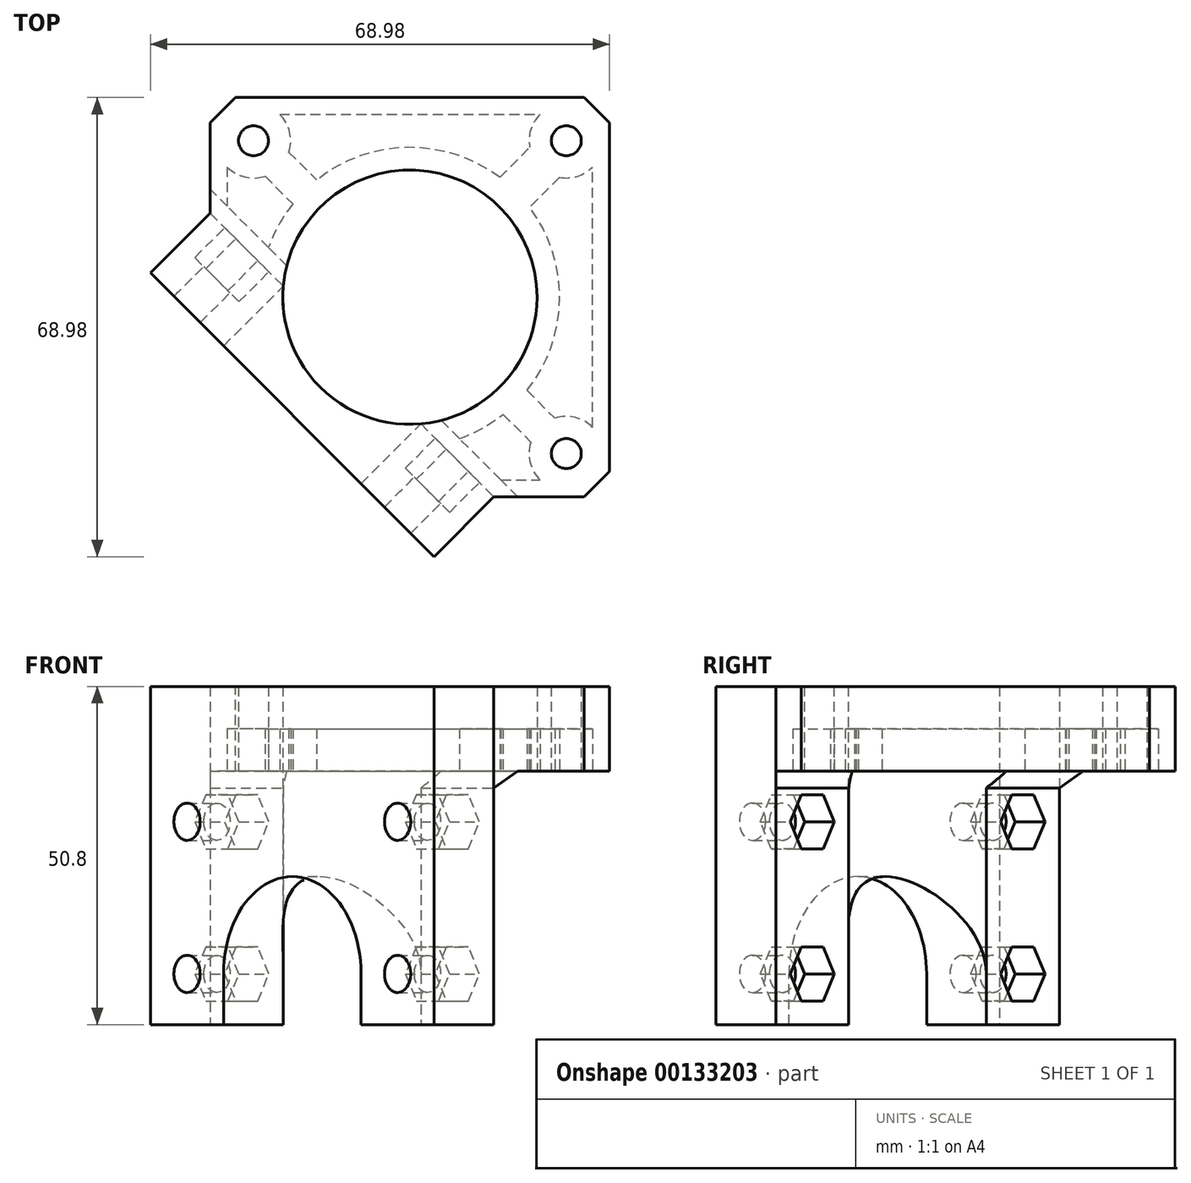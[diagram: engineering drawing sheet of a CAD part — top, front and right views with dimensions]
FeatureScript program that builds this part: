
annotation { "Feature Type Name" : "Feature", "Feature Type Description" : "" }
export const myFeature = defineFeature(function(context is Context, id is Id, definition is map)
    precondition{}
    {
        {
            var Q0;
            Q0=qCreatedBy(makeId("Top.planeOp"),FACE);
            var sketch = newSketch(context, id + "F0", { "sketchPlane" : qUnion([Q0])});
            skCircle(sketch, "E0", {"center": v(0, 0) * mm, "radius": 19.1 * mm});
            skLineSegment(sketch, "E1.bottom", {"start": v(-30, 30) * mm, "end": v(30, 30) * mm});
            skLineSegment(sketch, "E1.top", {"start": v(-30, -30) * mm, "end": v(30, -30) * mm});
            skLineSegment(sketch, "E1.left", {"start": v(-30, 30) * mm, "end": v(-30, -30) * mm});
            skLineSegment(sketch, "E1.right", {"start": v(30, 30) * mm, "end": v(30, -30) * mm});
            skCircle(sketch, "E2", {"center": v(-23.5, 23.5) * mm, "radius": 2.25 * mm});
            skCircle(sketch, "E3", {"center": v(-23.5, -23.5) * mm, "radius": 2.25 * mm});
            skCircle(sketch, "E4", {"center": v(23.5, -23.5) * mm, "radius": 2.25 * mm});
            skCircle(sketch, "E5", {"center": v(23.5, 23.5) * mm, "radius": 2.25 * mm});
            skLineSegment(sketch, "E6", {"start": v(0, -30) * mm, "end": v(0, 30) * mm, "construction": true});
            skLineSegment(sketch, "E7", {"start": v(-30, 0) * mm, "end": v(30, 0) * mm, "construction": true});
            skPoint(sketch, "E7.endSnap0", {"position": v(30, 0) * mm});
            skCircle(sketch, "E8", {"center": v(0, 0) * mm, "radius": 33.23 * mm, "construction": true});
            skSolve(sketch);
        }
        {
            var Q0;
            Q0=makeQuery(id+"F0.imprint","IMPRINT",FACE,{"disambiguationData":[TD([[makeQuery(id+"F0.imprint","IMPRINT",EDGE,{"derivedFrom":sQuery(id+"F0.wireOp",EDGE,"E0")}),-1.0]])]});
            extrude(context, id + "F1", {"entities" : qUnion([Q0]), "depth" : 50.8 * mm, "offsetDistance" : 25.4 * mm});
        }
        {
            var Q0;
            Q0=makeQuery(id+"F1.opExtrude","CAP_FACE",FACE,{"disambiguationData":[OSD([sQuery(id+"F0.wireOp",EDGE,"E0"),sQuery(id+"F0.wireOp",EDGE,"E1.bottom"),sQuery(id+"F0.wireOp",EDGE,"E1.top"),sQuery(id+"F0.wireOp",EDGE,"E1.left"),sQuery(id+"F0.wireOp",EDGE,"E1.right"),sQuery(id+"F0.wireOp",EDGE,"E2"),sQuery(id+"F0.wireOp",EDGE,"E3"),sQuery(id+"F0.wireOp",EDGE,"E4"),sQuery(id+"F0.wireOp",EDGE,"E5")])],"isStart":true});
            var sketch = newSketch(context, id + "F2", { "sketchPlane" : qUnion([Q0])});
            skLineSegment(sketch, "E9", {"start": v(-30, 5.35) * mm, "end": v(-5.35, 30) * mm});
            skLineSegment(sketch, "E10", {"start": v(-5.35, 30) * mm, "end": v(-30, 30) * mm});
            skLineSegment(sketch, "E11", {"start": v(-30, 5.35) * mm, "end": v(-30, 30) * mm});
            skSolve(sketch);
        }
        {
            var Q0;
            Q0 = qSketchRegion(id + "F2", true);
            var Q1;
            Q1=makeQuery(id+"F1.opExtrude","CAP_FACE",FACE,{"disambiguationData":[OSD([sQuery(id+"F0.wireOp",EDGE,"E0"),sQuery(id+"F0.wireOp",EDGE,"E1.bottom"),sQuery(id+"F0.wireOp",EDGE,"E1.top"),sQuery(id+"F0.wireOp",EDGE,"E1.left"),sQuery(id+"F0.wireOp",EDGE,"E1.right"),sQuery(id+"F0.wireOp",EDGE,"E2"),sQuery(id+"F0.wireOp",EDGE,"E3"),sQuery(id+"F0.wireOp",EDGE,"E4"),sQuery(id+"F0.wireOp",EDGE,"E5")])],"isStart":false});
            extrude(context, id + "F3", {"entities" : qUnion([Q0]), "operationType" : NewBodyOperationType.REMOVE, "endBound" : BoundingType.THROUGH_ALL, "oppositeDirection" : true, "depth" : 25.4 * mm, "endBoundEntityFace" : qUnion([Q1]), "offsetDistance" : 25.4 * mm});
        }
        {
            var Q0;
            Q0=qCreatedBy(makeId("Right.planeOp"),FACE);
            var Q1;
            Q1=qCreatedBy(makeId("Front.planeOp"),FACE);
            cPlane(context, id + "F4", {"entities" : qUnion([Q0, Q1]), "cplaneType" : CPlaneType.MID_PLANE, "offset" : 25.4 * mm, "flipAlignment" : true, "width" : 152.4 * mm, "height" : 152.4 * mm});
        }
        {
            var Q0;
            Q0=qCreatedBy(id+"F4.planeOp",FACE);
            var sketch = newSketch(context, id + "F5", { "sketchPlane" : qUnion([Q0])});
            skLineSegment(sketch, "E12.bottom", {"start": v(-12.3, 38.1) * mm, "end": v(42.43, 38.1) * mm});
            skLineSegment(sketch, "E12.top", {"start": v(-12.3, 0) * mm, "end": v(42.43, 0) * mm});
            skLineSegment(sketch, "E12.left", {"start": v(-12.3, 38.1) * mm, "end": v(-12.3, 0) * mm});
            skLineSegment(sketch, "E12.right", {"start": v(42.43, 38.1) * mm, "end": v(42.43, 0) * mm});
            skSolve(sketch);
        }
        {
            var Q0;
            Q0 = qSketchRegion(id + "F5", true);
            extrude(context, id + "F6", {"entities" : qUnion([Q0]), "operationType" : NewBodyOperationType.REMOVE, "oppositeDirection" : true, "depth" : 127 * mm, "offsetDistance" : 25.4 * mm, "symmetric" : true});
        }
        {
            var Q0;
            Q0=makeQuery(id+"F1.opExtrude","CAP_FACE",FACE,{"disambiguationData":[OSD([sQuery(id+"F0.wireOp",EDGE,"E0"),sQuery(id+"F0.wireOp",EDGE,"E1.bottom"),sQuery(id+"F0.wireOp",EDGE,"E1.top"),sQuery(id+"F0.wireOp",EDGE,"E1.left"),sQuery(id+"F0.wireOp",EDGE,"E1.right"),sQuery(id+"F0.wireOp",EDGE,"E2"),sQuery(id+"F0.wireOp",EDGE,"E3"),sQuery(id+"F0.wireOp",EDGE,"E4"),sQuery(id+"F0.wireOp",EDGE,"E5")])],"isStart":true});
            var sketch = newSketch(context, id + "F7", { "sketchPlane" : qUnion([Q0])});
            skLineSegment(sketch, "E13", {"start": v(-5.35, 30) * mm, "end": v(3.63, 38.98) * mm});
            skLineSegment(sketch, "E14", {"start": v(3.63, 38.98) * mm, "end": v(12.61, 30) * mm});
            skLineSegment(sketch, "E15", {"start": v(12.61, 30) * mm, "end": v(-5.35, 30) * mm});
            skLineSegment(sketch, "E16", {"start": v(-30, 5.35) * mm, "end": v(-38.98, -3.63) * mm});
            skLineSegment(sketch, "E17", {"start": v(-38.98, -3.63) * mm, "end": v(-30, -12.61) * mm});
            skLineSegment(sketch, "E18", {"start": v(-30, -12.61) * mm, "end": v(-30, 5.35) * mm});
            skSolve(sketch);
        }
        {
            var Q0;
            Q0 = qSketchRegion(id + "F7", true);
            var Q1;
            Q1=makeQuery(id+"F1.opExtrude","CAP_FACE",FACE,{"disambiguationData":[OSD([sQuery(id+"F0.wireOp",EDGE,"E0"),sQuery(id+"F0.wireOp",EDGE,"E1.bottom"),sQuery(id+"F0.wireOp",EDGE,"E1.top"),sQuery(id+"F0.wireOp",EDGE,"E1.left"),sQuery(id+"F0.wireOp",EDGE,"E1.right"),sQuery(id+"F0.wireOp",EDGE,"E2"),sQuery(id+"F0.wireOp",EDGE,"E3"),sQuery(id+"F0.wireOp",EDGE,"E4"),sQuery(id+"F0.wireOp",EDGE,"E5")])],"isStart":false});
            extrude(context, id + "F8", {"entities" : qUnion([Q0]), "operationType" : NewBodyOperationType.ADD, "endBound" : BoundingType.UP_TO_SURFACE, "oppositeDirection" : true, "depth" : 25.4 * mm, "endBoundEntityFace" : qUnion([Q1]), "offsetDistance" : 25.4 * mm});
        }
        {
            var Q0;
            {var subQ1=sQuery(id+"F0.wireOp",EDGE,"E1.top");Q0=makeQuery(id+"F6.boolean.opBoolean","COPY",FACE,{"disambiguationData":[TD([makeQuery(id+"F1.opExtrude","SWEPT_FACE",FACE,{"disambiguationData":[OSD([subQ1])]})])],"derivedFrom":makeQuery(id+"F6.opExtrude","SWEPT_FACE",FACE,{"disambiguationData":[OSD([sQuery(id+"F5.wireOp",EDGE,"E12.left")])]})});}
            var sketch = newSketch(context, id + "F9", { "sketchPlane" : qUnion([Q0])});
            skCircle(sketch, "E19", {"center": v(-22.38, 30.48) * mm, "radius": 2.8 * mm});
            skPoint(sketch, "E19.centerSnap0", {"position": v(-22.38, 38.1) * mm});
            skCircle(sketch, "E20", {"center": v(-22.38, 7.62) * mm, "radius": 2.8 * mm});
            skCircle(sketch, "E21", {"center": v(22.38, 7.62) * mm, "radius": 2.8 * mm});
            skCircle(sketch, "E22", {"center": v(22.38, 30.48) * mm, "radius": 2.8 * mm});
            skLineSegment(sketch, "E23", {"start": v(0, 39.15) * mm, "end": v(0, 1.92) * mm, "construction": true});
            skLineSegment(sketch, "E24", {"start": v(-22.38, 7.62) * mm, "end": v(-22.38, 30.48) * mm, "construction": true});
            skSolve(sketch);
        }
        {
            var Q0;
            Q0 = qSketchRegion(id + "F9", true);
            extrude(context, id + "F10", {"entities" : qUnion([Q0]), "operationType" : NewBodyOperationType.REMOVE, "endBound" : BoundingType.THROUGH_ALL, "oppositeDirection" : true, "depth" : 25.4 * mm, "offsetDistance" : 25.4 * mm});
        }
        {
            var Q0;
            Q0=makeQuery(id+"F1.opExtrude","SWEPT_EDGE",EDGE,{"disambiguationData":[OSD([sQuery(id+"F0.wireOp",EDGE,"E1.top"),sQuery(id+"F0.wireOp",EDGE,"E1.right")])]});
            var Q1;
            Q1=makeQuery(id+"F1.opExtrude","SWEPT_EDGE",EDGE,{"disambiguationData":[OSD([sQuery(id+"F0.wireOp",EDGE,"E1.bottom"),sQuery(id+"F0.wireOp",EDGE,"E1.right")])]});
            var Q2;
            Q2=makeQuery(id+"F1.opExtrude","SWEPT_EDGE",EDGE,{"disambiguationData":[OSD([sQuery(id+"F0.wireOp",EDGE,"E1.bottom"),sQuery(id+"F0.wireOp",EDGE,"E1.left")])]});
            chamfer(context, id + "F11", {"entities" : qUnion([Q0, Q1, Q2]), "width" : 3.8 * mm, "tangentPropagation" : true});
        }
        {
            var Q0;
            {var subQ1=sQuery(id+"F0.wireOp",EDGE,"E1.top");Q0=makeQuery(id+"F6.boolean.opBoolean","COPY",FACE,{"disambiguationData":[TD([makeQuery(id+"F1.opExtrude","SWEPT_FACE",FACE,{"disambiguationData":[OSD([subQ1])]})])],"derivedFrom":makeQuery(id+"F6.opExtrude","SWEPT_FACE",FACE,{"disambiguationData":[OSD([sQuery(id+"F5.wireOp",EDGE,"E12.left")])]})});}
            var sketch = newSketch(context, id + "F12", { "sketchPlane" : qUnion([Q0])});
            skCircle(sketch, "E25.cCircle", {"center": v(-22.38, 30.48) * mm, "radius": 4.06 * mm, "construction": true});
            skLineSegment(sketch, "E25.0", {"start": v(-17.68, 30.48) * mm, "end": v(-20.03, 26.42) * mm});
            skLineSegment(sketch, "E25.1", {"start": v(-20.03, 26.42) * mm, "end": v(-24.72, 26.42) * mm});
            skLineSegment(sketch, "E25.2", {"start": v(-24.72, 26.42) * mm, "end": v(-27.07, 30.48) * mm});
            skLineSegment(sketch, "E25.3", {"start": v(-27.07, 30.48) * mm, "end": v(-24.72, 34.54) * mm});
            skLineSegment(sketch, "E25.4", {"start": v(-24.72, 34.54) * mm, "end": v(-20.03, 34.54) * mm});
            skLineSegment(sketch, "E25.5", {"start": v(-20.03, 34.54) * mm, "end": v(-17.68, 30.48) * mm});
            skPoint(sketch, "E25.0.midPoint", {"position": v(-18.86, 28.45) * mm});
            skCircle(sketch, "E26.cCircle", {"center": v(-22.38, 7.62) * mm, "radius": 4.06 * mm, "construction": true});
            skLineSegment(sketch, "E26.0", {"start": v(-17.68, 7.62) * mm, "end": v(-20.03, 3.56) * mm});
            skLineSegment(sketch, "E26.1", {"start": v(-20.03, 3.56) * mm, "end": v(-24.72, 3.56) * mm});
            skLineSegment(sketch, "E26.2", {"start": v(-24.72, 3.56) * mm, "end": v(-27.07, 7.62) * mm});
            skLineSegment(sketch, "E26.3", {"start": v(-27.07, 7.62) * mm, "end": v(-24.72, 11.68) * mm});
            skLineSegment(sketch, "E26.4", {"start": v(-24.72, 11.68) * mm, "end": v(-20.03, 11.68) * mm});
            skLineSegment(sketch, "E26.5", {"start": v(-20.03, 11.68) * mm, "end": v(-17.68, 7.62) * mm});
            skPoint(sketch, "E26.0.midPoint", {"position": v(-18.86, 5.59) * mm});
            skCircle(sketch, "E27.cCircle", {"center": v(22.38, 7.62) * mm, "radius": 4.06 * mm, "construction": true});
            skLineSegment(sketch, "E27.0", {"start": v(27.07, 7.62) * mm, "end": v(24.72, 3.56) * mm});
            skLineSegment(sketch, "E27.1", {"start": v(24.72, 3.56) * mm, "end": v(20.03, 3.56) * mm});
            skLineSegment(sketch, "E27.2", {"start": v(20.03, 3.56) * mm, "end": v(17.68, 7.62) * mm});
            skLineSegment(sketch, "E27.3", {"start": v(17.68, 7.62) * mm, "end": v(20.03, 11.68) * mm});
            skLineSegment(sketch, "E27.4", {"start": v(20.03, 11.68) * mm, "end": v(24.72, 11.68) * mm});
            skLineSegment(sketch, "E27.5", {"start": v(24.72, 11.68) * mm, "end": v(27.07, 7.62) * mm});
            skPoint(sketch, "E27.0.midPoint", {"position": v(26.44, 7.62) * mm});
            skCircle(sketch, "E28.cCircle", {"center": v(22.38, 30.48) * mm, "radius": 4.06 * mm, "construction": true});
            skLineSegment(sketch, "E28.0", {"start": v(27.07, 30.48) * mm, "end": v(24.72, 26.42) * mm});
            skLineSegment(sketch, "E28.1", {"start": v(24.72, 26.42) * mm, "end": v(20.03, 26.42) * mm});
            skLineSegment(sketch, "E28.2", {"start": v(20.03, 26.42) * mm, "end": v(17.68, 30.48) * mm});
            skLineSegment(sketch, "E28.3", {"start": v(17.68, 30.48) * mm, "end": v(20.03, 34.54) * mm});
            skLineSegment(sketch, "E28.4", {"start": v(20.03, 34.54) * mm, "end": v(24.72, 34.54) * mm});
            skLineSegment(sketch, "E28.5", {"start": v(24.72, 34.54) * mm, "end": v(27.07, 30.48) * mm});
            skPoint(sketch, "E28.0.midPoint", {"position": v(25.9, 28.45) * mm});
            skSolve(sketch);
        }
        {
            var Q0;
            Q0 = qSketchRegion(id + "F12", true);
            extrude(context, id + "F13", {"entities" : qUnion([Q0]), "operationType" : NewBodyOperationType.REMOVE, "oppositeDirection" : true, "depth" : 6.35 * mm, "offsetDistance" : 25.4 * mm});
        }
        {
            var Q0;
            {var subQ0=sQuery(id+"F5.wireOp",EDGE,"E12.bottom");var subQ1=sQuery(id+"F5.wireOp",EDGE,"E12.left");Q0=makeQuery(id+"F6.boolean.opBoolean","COPY",EDGE,{"disambiguationData":[TD([makeQuery(id+"F1.opExtrude","SWEPT_FACE",FACE,{"disambiguationData":[OSD([sQuery(id+"F0.wireOp",EDGE,"E1.top")])]})])],"derivedFrom":makeQuery(id+"F6.opExtrude","SWEPT_EDGE",EDGE,{"disambiguationData":[OSD([subQ0,subQ1])]})});}
            var Q1;
            {var subQ0=sQuery(id+"F5.wireOp",EDGE,"E12.bottom");var subQ1=sQuery(id+"F5.wireOp",EDGE,"E12.left");Q1=makeQuery(id+"F6.boolean.opBoolean","COPY",EDGE,{"disambiguationData":[TD([makeQuery(id+"F1.opExtrude","SWEPT_FACE",FACE,{"disambiguationData":[OSD([sQuery(id+"F0.wireOp",EDGE,"E1.left")])]})])],"derivedFrom":makeQuery(id+"F6.opExtrude","SWEPT_EDGE",EDGE,{"disambiguationData":[OSD([subQ0,subQ1])]})});}
            chamfer(context, id + "F14", {"entities" : qUnion([Q0, Q1]), "width" : 2.54 * mm, "tangentPropagation" : true});
        }
        {
            var Q0;
            {var subQ1=sQuery(id+"F0.wireOp",EDGE,"E1.top");Q0=makeQuery(id+"F6.boolean.opBoolean","COPY",FACE,{"disambiguationData":[TD([makeQuery(id+"F1.opExtrude","SWEPT_FACE",FACE,{"disambiguationData":[OSD([subQ1])]})])],"derivedFrom":makeQuery(id+"F6.opExtrude","SWEPT_FACE",FACE,{"disambiguationData":[OSD([sQuery(id+"F5.wireOp",EDGE,"E12.left")])]})});}
            var sketch = newSketch(context, id + "F15", { "sketchPlane" : qUnion([Q0])});
            skArc(sketch, "E29", {"start": v(14.62, 7.62) * mm, "mid": v(0, 22.24) * mm, "end": v(-14.62, 7.62) * mm});
            skLineSegment(sketch, "E30", {"start": v(-14.62, 7.62) * mm, "end": v(-14.62, 0) * mm});
            skLineSegment(sketch, "E31", {"start": v(-14.62, 0) * mm, "end": v(14.62, 0) * mm});
            skLineSegment(sketch, "E32", {"start": v(14.62, 0) * mm, "end": v(14.62, 7.62) * mm});
            skSolve(sketch);
        }
        {
            var Q0;
            Q0 = qSketchRegion(id + "F15", true);
            extrude(context, id + "F16", {"entities" : qUnion([Q0]), "operationType" : NewBodyOperationType.REMOVE, "oppositeDirection" : true, "depth" : 25.4 * mm, "offsetDistance" : 25.4 * mm});
        }
        {
            var Q0;
            Q0=makeQuery(id+"F6.boolean.opBoolean","COPY",FACE,{"derivedFrom":makeQuery(id+"F6.opExtrude","SWEPT_FACE",FACE,{"disambiguationData":[OSD([sQuery(id+"F5.wireOp",EDGE,"E12.bottom")])]})});
            var sketch = newSketch(context, id + "F17", { "sketchPlane" : qUnion([Q0])});
            skArc(sketch, "E33", {"start": v(14.01, 17.6) * mm, "mid": v(10.88, 19.7) * mm, "end": v(7.44, 21.23) * mm});
            skLineSegment(sketch, "E34", {"start": v(27.46, 19.56) * mm, "end": v(27.46, -19.56) * mm});
            skLineSegment(sketch, "E35", {"start": v(-19.56, -27.46) * mm, "end": v(19.56, -27.46) * mm});
            skArc(sketch, "E36", {"start": v(-19.56, -27.46) * mm, "mid": v(-18.07, -24.81) * mm, "end": v(-18.18, -21.78) * mm});
            skArc(sketch, "E37", {"start": v(27.46, -19.56) * mm, "mid": v(25.17, -18.17) * mm, "end": v(22.5, -18) * mm});
            skArc(sketch, "E38", {"start": v(21.78, 18.18) * mm, "mid": v(24.81, 18.07) * mm, "end": v(27.46, 19.56) * mm});
            skLineSegment(sketch, "E39", {"start": v(-21.78, -18.18) * mm, "end": v(-17.6, -14.01) * mm});
            skLineSegment(sketch, "E40", {"start": v(-18.18, -21.78) * mm, "end": v(-14.01, -17.6) * mm});
            skLineSegment(sketch, "E41.trimOffspring", {"start": v(17.6, 14.01) * mm, "end": v(21.78, 18.18) * mm});
            skLineSegment(sketch, "E42.trimOffspring", {"start": v(14.01, 17.6) * mm, "end": v(18.18, 21.78) * mm});
            skArc(sketch, "E43.trimOffspring", {"start": v(-14.01, -17.6) * mm, "mid": v(-0.32, -22.5) * mm, "end": v(13.5, -18) * mm});
            skLineSegment(sketch, "E44", {"start": v(13.5, -18) * mm, "end": v(18, -22.5) * mm});
            skLineSegment(sketch, "E45", {"start": v(22.5, -18) * mm, "end": v(18, -13.5) * mm});
            skPoint(sketch, "E45.endSnap0", {"position": v(13.5, -13.5) * mm});
            skArc(sketch, "E46", {"start": v(-21.78, -18.18) * mm, "mid": v(-24.81, -18.07) * mm, "end": v(-27.46, -19.56) * mm});
            skArc(sketch, "E47", {"start": v(19.56, 27.46) * mm, "mid": v(18.07, 24.81) * mm, "end": v(18.18, 21.78) * mm});
            skLineSegment(sketch, "E48", {"start": v(13.67, 27.46) * mm, "end": v(19.56, 27.46) * mm});
            skLineSegment(sketch, "E49", {"start": v(-27.46, -19.56) * mm, "end": v(-27.46, -13.67) * mm});
            skLineSegment(sketch, "E50.0", {"start": v(13.67, 27.46) * mm, "end": v(7.44, 21.23) * mm});
            skLineSegment(sketch, "E51.0", {"start": v(-21.23, -7.44) * mm, "end": v(-27.46, -13.67) * mm});
            skArc(sketch, "E52.trimOffspring", {"start": v(-21.23, -7.44) * mm, "mid": v(-19.7, -10.88) * mm, "end": v(-17.6, -14.01) * mm});
            skLineSegment(sketch, "E53", {"start": v(0, 0) * mm, "end": v(36, -36) * mm, "construction": true});
            skArc(sketch, "E54.trimOffspring", {"start": v(18, -22.5) * mm, "mid": v(18.17, -25.17) * mm, "end": v(19.56, -27.46) * mm});
            skArc(sketch, "E55.trimOffspring", {"start": v(18, -13.5) * mm, "mid": v(22.5, 0.32) * mm, "end": v(17.6, 14.01) * mm});
            skLineSegment(sketch, "E56", {"start": v(-23.5, -23.5) * mm, "end": v(23.5, 23.5) * mm, "construction": true});
            skSolve(sketch);
        }
        {
            var Q0;
            Q0 = qSketchRegion(id + "F17", true);
            extrude(context, id + "F18", {"entities" : qUnion([Q0]), "operationType" : NewBodyOperationType.REMOVE, "oppositeDirection" : true, "depth" : 6.35 * mm, "offsetDistance" : 25.4 * mm});
        }
    });
